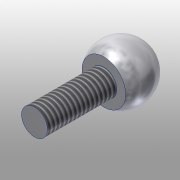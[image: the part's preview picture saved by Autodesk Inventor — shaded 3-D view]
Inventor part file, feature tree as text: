
AUTODESK INVENTOR PART (.ipt)
format: ipt  version: 2016 (Build 200138000, 138)  size: 139,776 bytes
history: native  units: mm
features: sketch x4, extrude x3, revolve x1, thread x1, projected_geometry x1
ambient origin geometry x8: Origin, YZ Plane, XZ Plane, XY Plane, X Axis, Y Axis, Z Axis, Center Point
bodies: Solid1 (feature_tree)
feature tree (10):
  revolve  "Revolution1"  Angle=90.0deg
  extrude  "Extrusion1"  Depth=10.0mm TaperAngle=0.0deg
  extrude  "Extrusion2"  Depth=8.0mm TaperAngle=0.0deg
  thread  "Thread1"  [1 undecoded]
  extrude  "Extrusion3"  Depth=2.0mm TaperAngle=0.0deg
  sketch  "Sketch1"  dims[d0=6.4mm d1=90.0deg]
  sketch  "Sketch2"  dims[d2=4.8mm d3=10.0mm d4=0.0mm]
  sketch  "Sketch3"  dims[d5=3.0mm d6=8.0mm d7=0.0mm d8=3.0mm]
  sketch  "Sketch4"  dims[d9=10.0mm d10=0.0mm d11=2.0mm d12=0.0mm]
  projected_geometry  "Project Cut Edges1"
note: 1 required parameter value undecoded (feature->parameter linkage not recoverable at this tier; creation-order binding heuristic only, values carry confidence <= 0.55)
